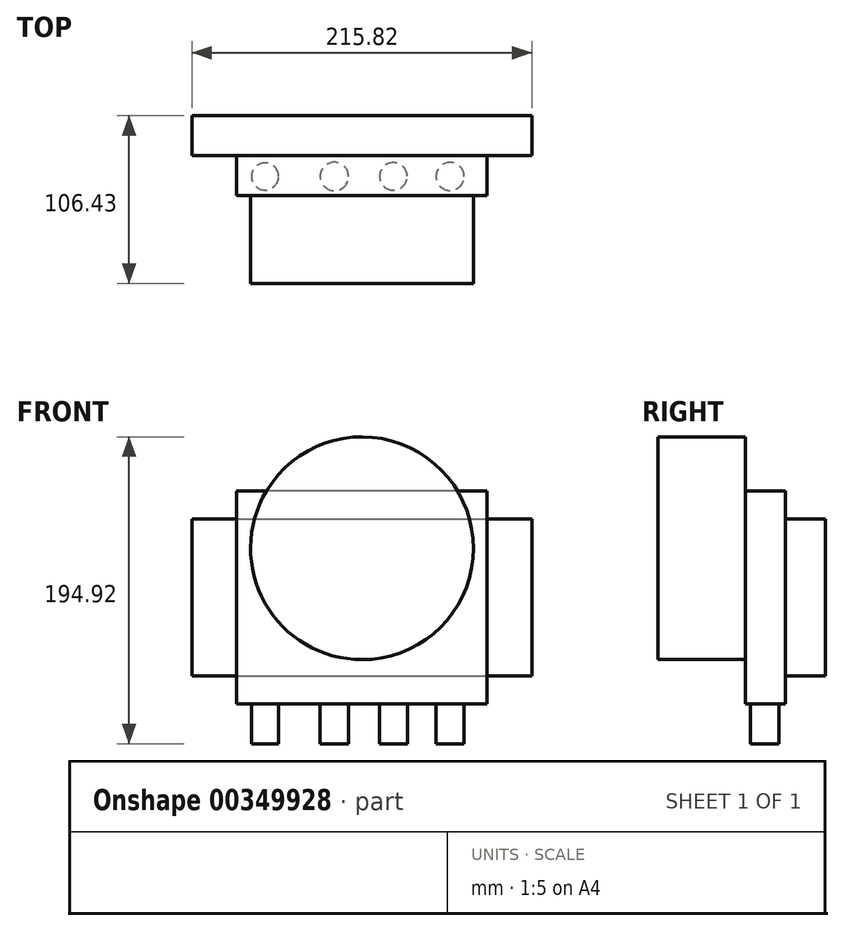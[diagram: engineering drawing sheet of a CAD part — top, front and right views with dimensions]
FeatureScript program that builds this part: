
annotation { "Feature Type Name" : "Feature", "Feature Type Description" : "" }
export const myFeature = defineFeature(function(context is Context, id is Id, definition is map)
    precondition{}
    {
        {
            var Q0;
            Q0=qCreatedBy(makeId("Front.planeOp"),FACE);
            var sketch = newSketch(context, id + "F0", { "sketchPlane" : qUnion([Q0])});
            skLineSegment(sketch, "E0.bottom", {"start": v(79.56, -67.53) * mm, "end": v(-79.56, -67.53) * mm});
            skLineSegment(sketch, "E0.top", {"start": v(79.56, 67.53) * mm, "end": v(-79.56, 67.53) * mm});
            skLineSegment(sketch, "E0.left", {"start": v(79.56, -67.53) * mm, "end": v(79.56, 67.53) * mm});
            skLineSegment(sketch, "E0.right", {"start": v(-79.56, -67.53) * mm, "end": v(-79.56, 67.53) * mm});
            skPoint(sketch, "E0.middle", {"position": v(0, 0) * mm});
            skSolve(sketch);
        }
        {
            var Q0;
            Q0 = qSketchRegion(id + "F0", true);
            extrude(context, id + "F1", {"entities" : qUnion([Q0]), "depth" : 25.4 * mm, "offsetDistance" : 25.4 * mm});
        }
        {
            var Q0;
            Q0=makeQuery(id+"F1.opExtrude","CAP_FACE",FACE,{"disambiguationData":[OSD([sQuery(id+"F0.wireOp",EDGE,"E0.bottom"),sQuery(id+"F0.wireOp",EDGE,"E0.top"),sQuery(id+"F0.wireOp",EDGE,"E0.left"),sQuery(id+"F0.wireOp",EDGE,"E0.right")])],"isStart":false});
            var sketch = newSketch(context, id + "F2", { "sketchPlane" : qUnion([Q0])});
            skCircle(sketch, "E1", {"center": v(0, 31.22) * mm, "radius": 70.76 * mm});
            skSolve(sketch);
        }
        {
            var Q0;
            Q0 = qSketchRegion(id + "F2", true);
            extrude(context, id + "F3", {"entities" : qUnion([Q0]), "operationType" : NewBodyOperationType.ADD, "depth" : 55.63 * mm, "offsetDistance" : 25.4 * mm});
        }
        {
            var Q0;
            Q0=makeQuery(id+"F1.opExtrude","SWEPT_FACE",FACE,{"disambiguationData":[OSD([sQuery(id+"F0.wireOp",EDGE,"E0.bottom")])]});
            var sketch = newSketch(context, id + "F4", { "sketchPlane" : qUnion([Q0])});
            skCircle(sketch, "E2", {"center": v(-61.6, 13.12) * mm, "radius": 8.64 * mm});
            skCircle(sketch, "E3", {"center": v(-17.53, 13.12) * mm, "radius": 9.02 * mm});
            skCircle(sketch, "E4", {"center": v(20.02, 13.12) * mm, "radius": 8.79 * mm});
            skCircle(sketch, "E5", {"center": v(56.01, 13.12) * mm, "radius": 8.93 * mm});
            skSolve(sketch);
        }
        {
            var Q0;
            Q0 = qSketchRegion(id + "F4", true);
            extrude(context, id + "F5", {"entities" : qUnion([Q0]), "operationType" : NewBodyOperationType.ADD, "depth" : 25.4 * mm, "offsetDistance" : 25.4 * mm});
        }
        {
            var Q0;
            Q0=makeQuery(id+"F1.opExtrude","CAP_FACE",FACE,{"disambiguationData":[OSD([sQuery(id+"F0.wireOp",EDGE,"E0.bottom"),sQuery(id+"F0.wireOp",EDGE,"E0.top"),sQuery(id+"F0.wireOp",EDGE,"E0.left"),sQuery(id+"F0.wireOp",EDGE,"E0.right")])],"isStart":true});
            var sketch = newSketch(context, id + "F6", { "sketchPlane" : qUnion([Q0])});
            skLineSegment(sketch, "E6.bottom", {"start": v(107.9, -49.9) * mm, "end": v(-107.9, -49.9) * mm});
            skLineSegment(sketch, "E6.top", {"start": v(107.9, 49.9) * mm, "end": v(-107.9, 49.9) * mm});
            skLineSegment(sketch, "E6.left", {"start": v(107.9, -49.9) * mm, "end": v(107.9, 49.9) * mm});
            skLineSegment(sketch, "E6.right", {"start": v(-107.9, -49.9) * mm, "end": v(-107.9, 49.9) * mm});
            skPoint(sketch, "E6.middle", {"position": v(0, 0) * mm});
            skSolve(sketch);
        }
        {
            var Q0;
            Q0 = qSketchRegion(id + "F6", true);
            extrude(context, id + "F7", {"entities" : qUnion([Q0]), "operationType" : NewBodyOperationType.ADD, "depth" : 25.4 * mm, "offsetDistance" : 25.4 * mm});
        }
    });
